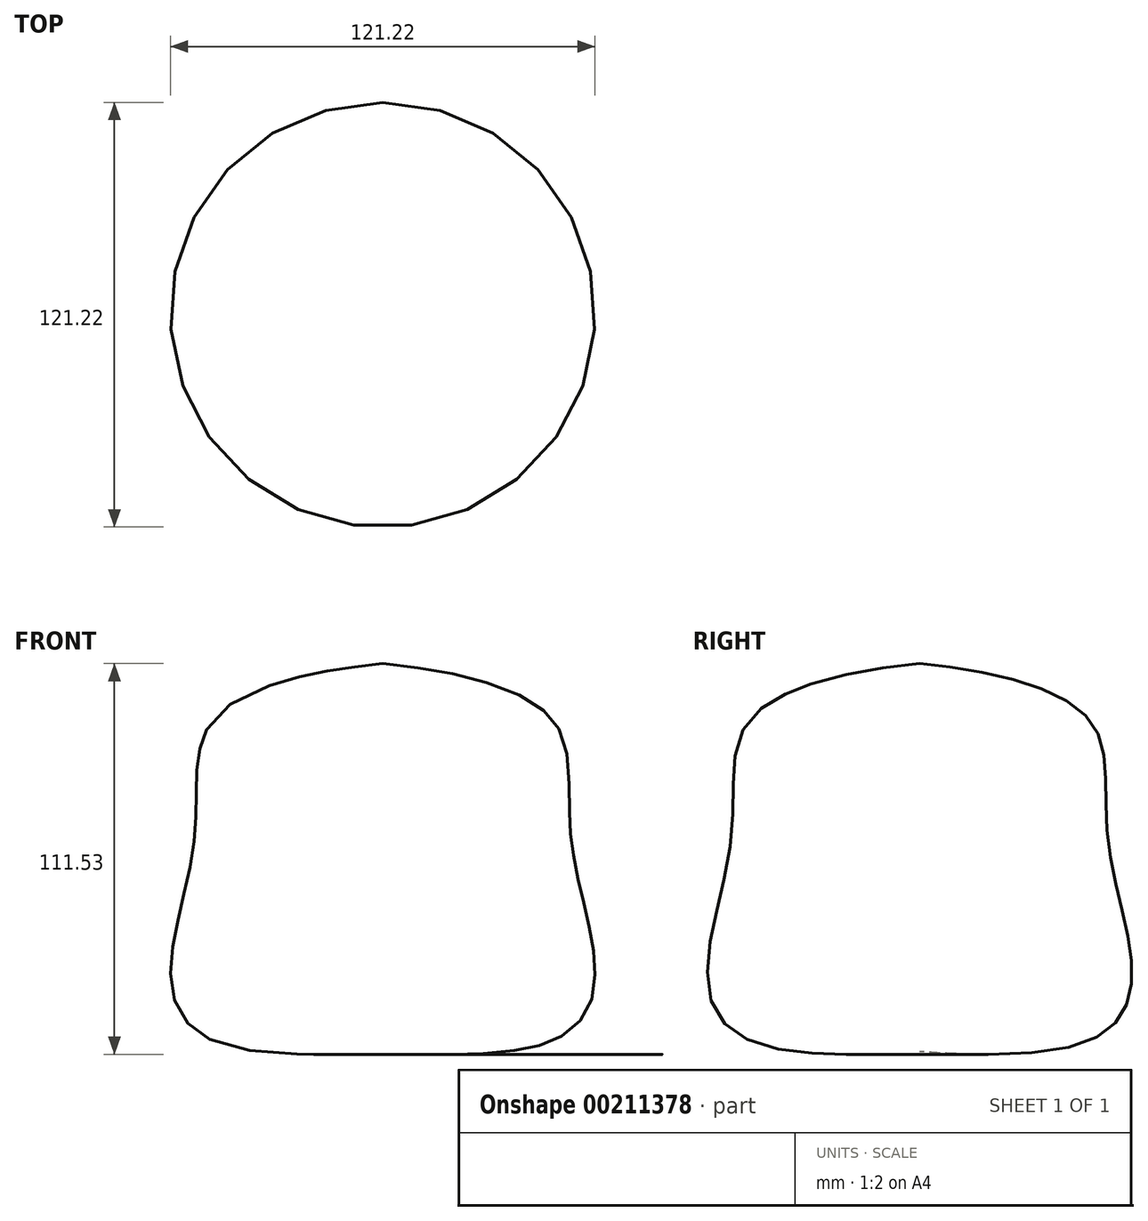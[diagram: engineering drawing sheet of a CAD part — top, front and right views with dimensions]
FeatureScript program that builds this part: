
annotation { "Feature Type Name" : "Feature", "Feature Type Description" : "" }
export const myFeature = defineFeature(function(context is Context, id is Id, definition is map)
    precondition{}
    {
        {
            var Q0;
            Q0=qCreatedBy(makeId("Right.planeOp"),FACE);
            var sketch = newSketch(context, id + "F0", { "sketchPlane" : qUnion([Q0])});
            skFitSpline(sketch, "E0", {"points": [v(-38.25, 46.46) * mm, v(4.3, 44.85) * mm, v(48.75, 28.96) * mm, v(53.6, -3.37) * mm, v(60.6, -42.7) * mm, v(43.64, -63.97) * mm, v(-28.55, -62.63) * mm, v(-28.82, -62.63) * mm], "startDerivative": vector(241.5, 2.34) * mm, "endDerivative": vector(-8.05, -1.84) * mm});
            skLineSegment(sketch, "E1", {"start": v(0, 62.9) * mm, "end": v(0, -75.55) * mm});
            skSolve(sketch);
        }
        {
            var Q0;
            {var subQ0=sQuery(id+"F0.wireOp",EDGE,"E1");var subQ1=sQuery(id+"F0.wireOp",EDGE,"E0");var subQ2=makeQuery(id+"F0.imprint","INTERSECT",VERTEX,{"disambiguationData":[OD(0.0)],"derivedFrom":[subQ1,subQ0]});Q0=makeQuery(id+"F0.imprint","IMPRINT",FACE,{"disambiguationData":[TD([[makeQuery(id+"F0.imprint","IMPRINT",EDGE,{"disambiguationData":[TD([[subQ2,1.0]])],"derivedFrom":subQ1}),-1.0]])]});}
            var Q1;
            Q1=sQuery(id+"F0.wireOp",EDGE,"E1");
            revolve(context, id + "F1", {"entities" : qUnion([Q0]), "axis" : qUnion([Q1]), "revolveType" : RevolveType.FULL});
        }
    });
